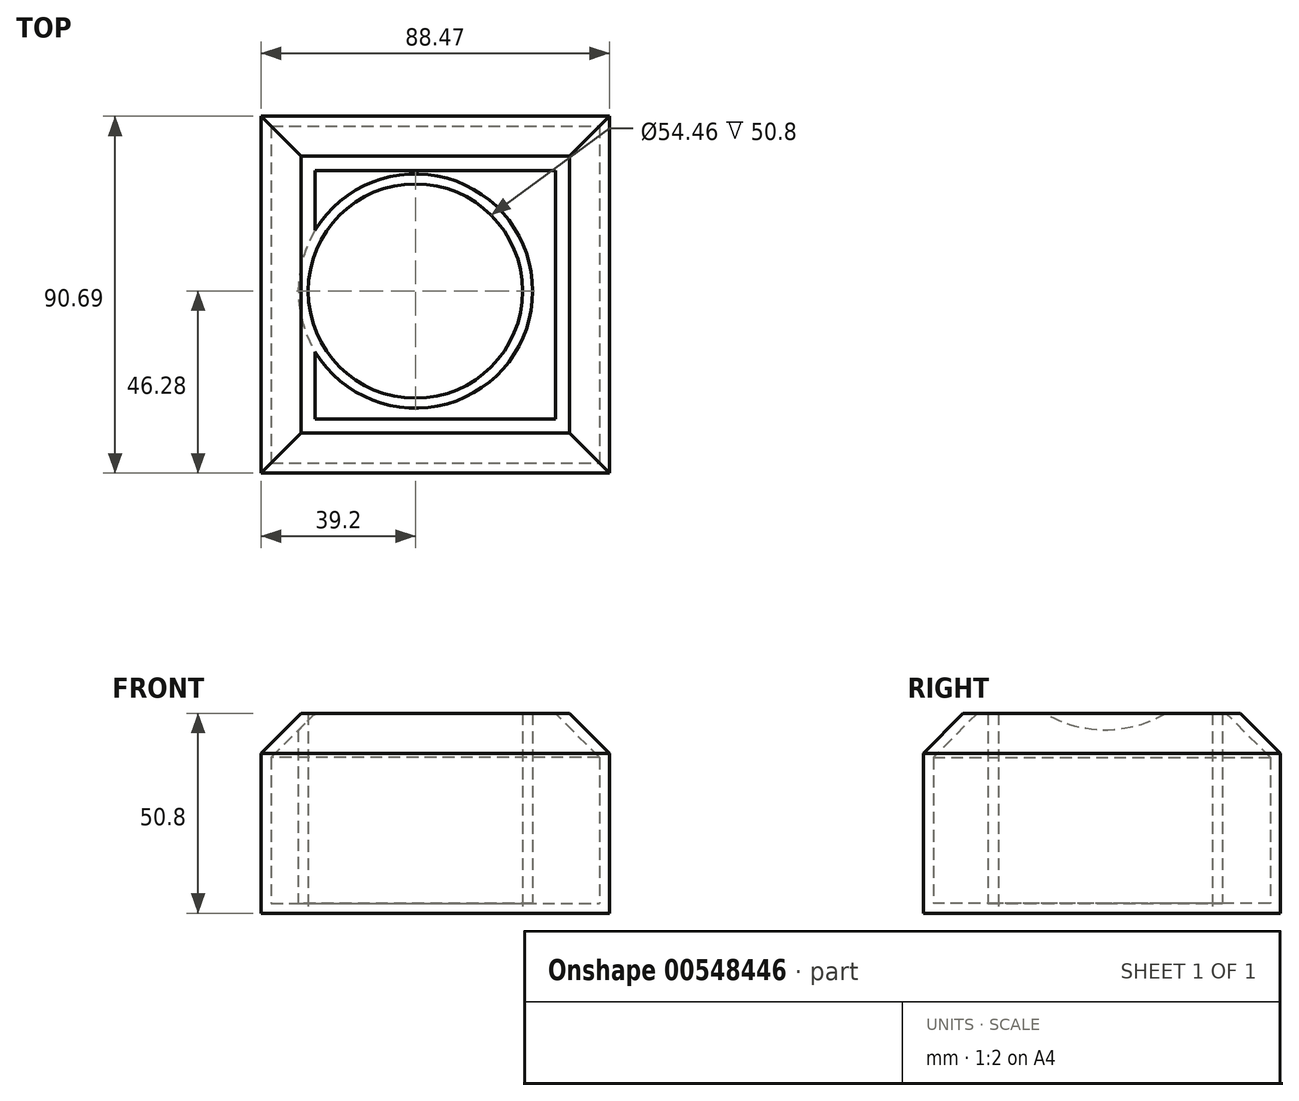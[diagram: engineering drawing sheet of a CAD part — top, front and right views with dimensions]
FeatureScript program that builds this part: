
annotation { "Feature Type Name" : "Feature", "Feature Type Description" : "" }
export const myFeature = defineFeature(function(context is Context, id is Id, definition is map)
    precondition{}
    {
        {
            var Q0;
            Q0=qCreatedBy(makeId("Top.planeOp"),FACE);
            var sketch = newSketch(context, id + "F0", { "sketchPlane" : qUnion([Q0])});
            skLineSegment(sketch, "E0.bottom", {"start": v(-39.2, 44.4) * mm, "end": v(49.27, 44.4) * mm});
            skLineSegment(sketch, "E0.top", {"start": v(-39.2, -46.28) * mm, "end": v(49.27, -46.28) * mm});
            skLineSegment(sketch, "E0.left", {"start": v(-39.2, 44.4) * mm, "end": v(-39.2, -46.28) * mm});
            skLineSegment(sketch, "E0.right", {"start": v(49.27, 44.4) * mm, "end": v(49.27, -46.28) * mm});
            skCircle(sketch, "E1", {"center": v(0, 0) * mm, "radius": 27.23 * mm});
            skSolve(sketch);
        }
        {
            var Q0;
            Q0=makeQuery(id+"F0.imprint","IMPRINT",FACE,{"disambiguationData":[TD([[makeQuery(id+"F0.imprint","IMPRINT",EDGE,{"derivedFrom":sQuery(id+"F0.wireOp",EDGE,"E0.bottom")}),-1.0]])]});
            extrude(context, id + "F1", {"entities" : qUnion([Q0]), "depth" : 50.8 * mm, "offsetDistance" : 25.4 * mm});
        }
        {
            var Q0;
            Q0=makeQuery(id+"F1.opExtrude","CAP_EDGE",EDGE,{"disambiguationData":[OSD([sQuery(id+"F0.wireOp",EDGE,"E0.top")])],"isStart":false});
            var Q1;
            Q1=makeQuery(id+"F1.opExtrude","CAP_EDGE",EDGE,{"disambiguationData":[OSD([sQuery(id+"F0.wireOp",EDGE,"E0.left")])],"isStart":false});
            var Q2;
            Q2=makeQuery(id+"F1.opExtrude","CAP_EDGE",EDGE,{"disambiguationData":[OSD([sQuery(id+"F0.wireOp",EDGE,"E0.bottom")])],"isStart":false});
            var Q3;
            Q3=makeQuery(id+"F1.opExtrude","CAP_EDGE",EDGE,{"disambiguationData":[OSD([sQuery(id+"F0.wireOp",EDGE,"E0.right")])],"isStart":false});
            chamfer(context, id + "F2", {"entities" : qUnion([Q0, Q1, Q2, Q3]), "width" : 10.16 * mm, "tangentPropagation" : true});
        }
        {
            var Q0;
            Q0=makeQuery(id+"F1.opExtrude","CAP_FACE",FACE,{"disambiguationData":[OSD([sQuery(id+"F0.wireOp",EDGE,"E0.bottom"),sQuery(id+"F0.wireOp",EDGE,"E0.top"),sQuery(id+"F0.wireOp",EDGE,"E0.left"),sQuery(id+"F0.wireOp",EDGE,"E0.right"),sQuery(id+"F0.wireOp",EDGE,"E1")])],"isStart":false});
            shell(context, id + "F3", {"entities" : qUnion([Q0]), "thickness" : 2.54 * mm});
        }
    });
